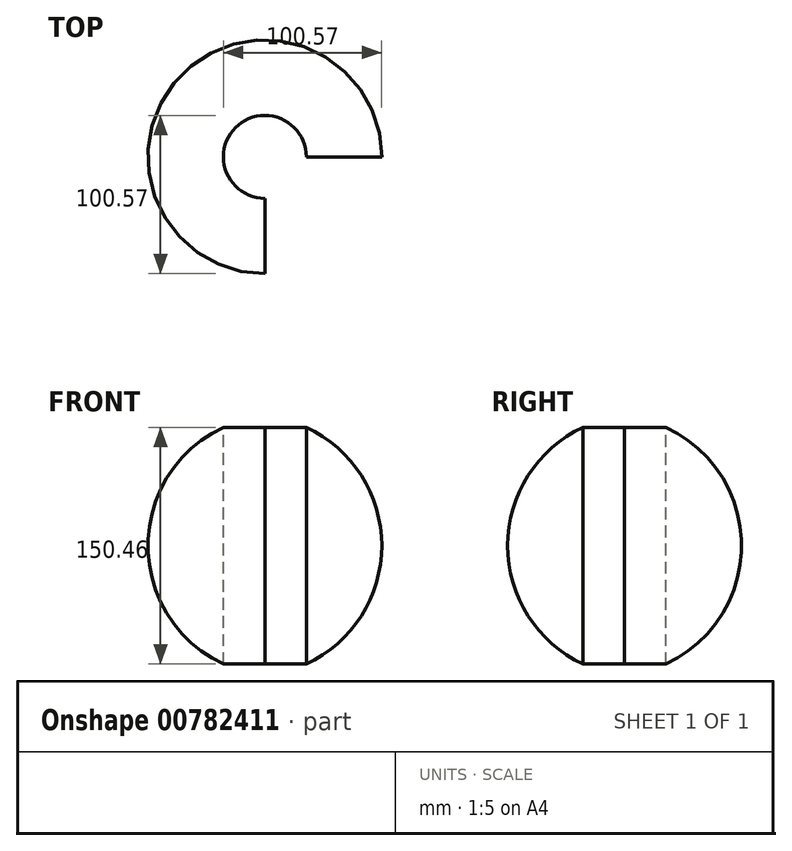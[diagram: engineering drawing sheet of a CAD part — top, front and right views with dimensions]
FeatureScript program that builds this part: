
annotation { "Feature Type Name" : "Feature", "Feature Type Description" : "" }
export const myFeature = defineFeature(function(context is Context, id is Id, definition is map)
    precondition{}
    {
        {
            var Q0;
            Q0=qCreatedBy(makeId("Right.planeOp"),FACE);
            var sketch = newSketch(context, id + "F0", { "sketchPlane" : qUnion([Q0])});
            skLineSegment(sketch, "E0", {"start": v(0, 0) * mm, "end": v(0, -165.1) * mm});
            skArc(sketch, "E1", {"start": v(0, 0) * mm, "mid": v(-74.24, -82.55) * mm, "end": v(0, -165.1) * mm});
            skSolve(sketch);
        }
        {
            var Q0;
            Q0 = qSketchRegion(id + "F0", true);
            var Q1;
            Q1=sQuery(id+"F0.wireOp",EDGE,"E0");
            revolve(context, id + "F1", {"surfaceOperationType" : NewSurfaceOperationType.NEW, "entities" : qUnion([Q0]), "axis" : qUnion([Q1]), "revolveType" : RevolveType.ONE_DIRECTION, "angle" : 270 * degree});
        }
        {
            var Q0;
            Q0=qCreatedBy(makeId("Top.planeOp"),FACE);
            var sketch = newSketch(context, id + "F2", { "sketchPlane" : qUnion([Q0])});
            skCircle(sketch, "E2", {"center": v(0, 0) * mm, "radius": 26.33 * mm});
            skSolve(sketch);
        }
        {
            var Q0;
            Q0 = qSketchRegion(id + "F2", true);
            extrude(context, id + "F3", {"entities" : qUnion([Q0]), "operationType" : NewBodyOperationType.REMOVE, "endBound" : BoundingType.THROUGH_ALL, "oppositeDirection" : true, "depth" : 25.4 * mm, "offsetDistance" : 25.4 * mm});
        }
    });
